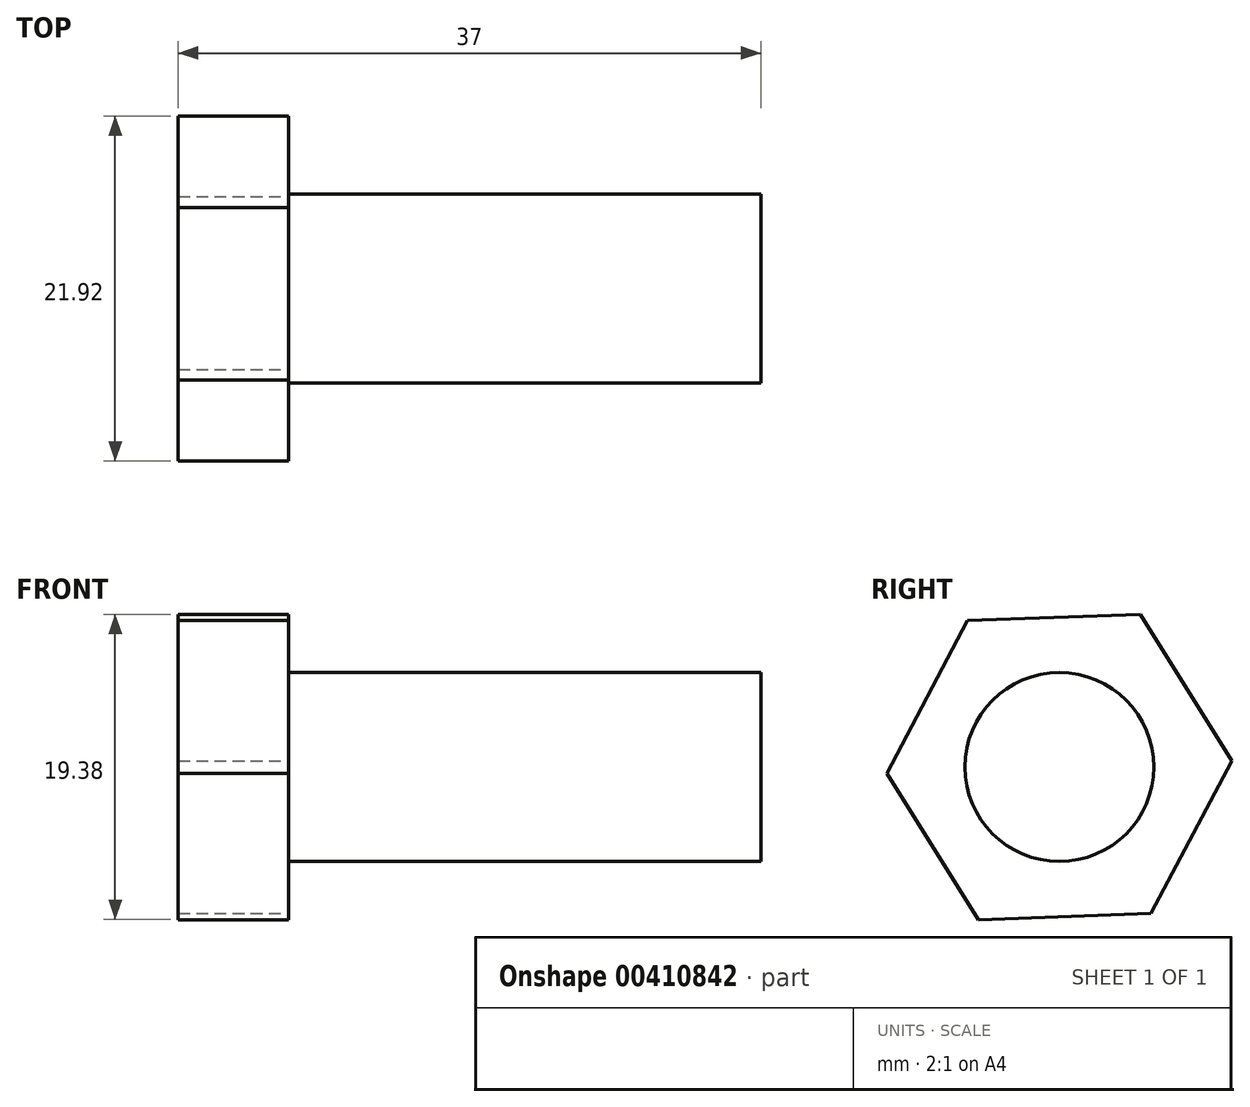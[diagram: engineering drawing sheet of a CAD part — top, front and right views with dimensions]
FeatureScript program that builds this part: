
annotation { "Feature Type Name" : "Feature", "Feature Type Description" : "" }
export const myFeature = defineFeature(function(context is Context, id is Id, definition is map)
    precondition{}
    {
        {
            var Q0;
            Q0=qCreatedBy(makeId("Front.planeOp"),FACE);
            var sketch = newSketch(context, id + "F0", { "sketchPlane" : qUnion([Q0])});
            skLineSegment(sketch, "E0.bottom", {"start": v(0, 0) * mm, "end": v(30, 0) * mm});
            skLineSegment(sketch, "E0.top", {"start": v(0, 6) * mm, "end": v(30, 6) * mm});
            skLineSegment(sketch, "E0.left", {"start": v(0, 0) * mm, "end": v(0, 6) * mm});
            skLineSegment(sketch, "E0.right", {"start": v(30, 0) * mm, "end": v(30, 6) * mm});
            skSolve(sketch);
        }
        {
            var Q0;
            Q0=makeQuery(id+"F0.imprint","IMPRINT",FACE,{"disambiguationData":[TD([[makeQuery(id+"F0.imprint","IMPRINT",EDGE,{"derivedFrom":sQuery(id+"F0.wireOp",EDGE,"E0.bottom")}),1.0]])]});
            var Q1;
            Q1=sQuery(id+"F0.wireOp",EDGE,"E0.bottom");
            revolve(context, id + "F1", {"entities" : qUnion([Q0]), "axis" : qUnion([Q1]), "revolveType" : RevolveType.FULL});
        }
        {
            var Q0;
            Q0=makeQuery(id+"F1.opRevolve","SWEPT_FACE",FACE,{"disambiguationData":[OSD([sQuery(id+"F0.wireOp",EDGE,"E0.left")])]});
            var sketch = newSketch(context, id + "F2", { "sketchPlane" : qUnion([Q0])});
            skCircle(sketch, "E1.cCircle", {"center": v(0, 0) * mm, "radius": 9.5 * mm, "construction": true});
            skLineSegment(sketch, "E1.0", {"start": v(5.82, 9.3) * mm, "end": v(10.96, -0.4) * mm});
            skLineSegment(sketch, "E1.1", {"start": v(10.96, -0.4) * mm, "end": v(5.14, -9.7) * mm});
            skLineSegment(sketch, "E1.2", {"start": v(5.14, -9.7) * mm, "end": v(-5.82, -9.3) * mm});
            skLineSegment(sketch, "E1.3", {"start": v(-5.82, -9.3) * mm, "end": v(-10.96, 0.4) * mm});
            skLineSegment(sketch, "E1.4", {"start": v(-10.96, 0.4) * mm, "end": v(-5.14, 9.7) * mm});
            skLineSegment(sketch, "E1.5", {"start": v(-5.14, 9.7) * mm, "end": v(5.82, 9.3) * mm});
            skPoint(sketch, "E1.0.midPoint", {"position": v(8.4, 4.45) * mm});
            skSolve(sketch);
        }
        {
            var Q0;
            Q0 = qSketchRegion(id + "F2", true);
            extrude(context, id + "F3", {"entities" : qUnion([Q0]), "operationType" : NewBodyOperationType.ADD, "depth" : 7 * mm});
        }
    });
